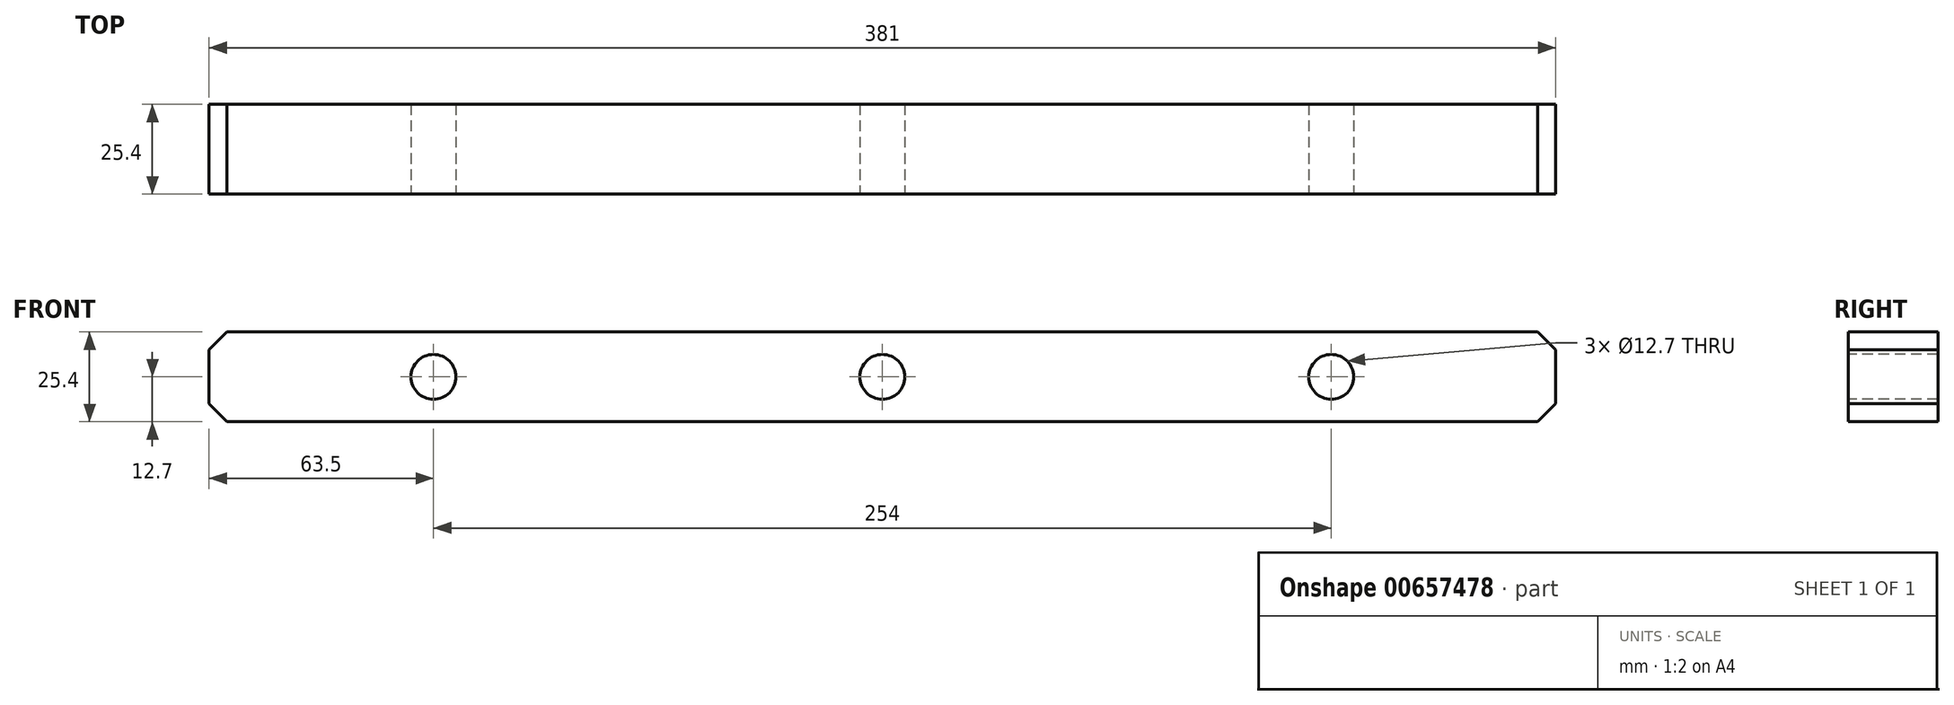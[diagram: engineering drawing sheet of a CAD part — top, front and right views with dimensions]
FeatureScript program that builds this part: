
annotation { "Feature Type Name" : "Feature", "Feature Type Description" : "" }
export const myFeature = defineFeature(function(context is Context, id is Id, definition is map)
    precondition{}
    {
        {
            var Q0;
            Q0=qCreatedBy(makeId("Front.planeOp"),FACE);
            var sketch = newSketch(context, id + "F0", { "sketchPlane" : qUnion([Q0])});
            skLineSegment(sketch, "E0", {"start": v(0, 0) * mm, "end": v(190.5, 0) * mm});
            skLineSegment(sketch, "E1", {"start": v(0, 0) * mm, "end": v(-190.5, 0) * mm});
            skLineSegment(sketch, "E2", {"start": v(-190.5, 0) * mm, "end": v(-190.5, 25.4) * mm});
            skLineSegment(sketch, "E3", {"start": v(190.5, 0) * mm, "end": v(190.5, 25.4) * mm});
            skLineSegment(sketch, "E4", {"start": v(190.5, 25.4) * mm, "end": v(-190.5, 25.4) * mm});
            skSolve(sketch);
        }
        {
            var Q0;
            Q0=makeQuery(id+"F0.imprint","IMPRINT",FACE,{"disambiguationData":[TD([[makeQuery(id+"F0.imprint","IMPRINT",EDGE,{"derivedFrom":sQuery(id+"F0.wireOp",EDGE,"E0")}),1.0]])]});
            extrude(context, id + "F1", {"entities" : qUnion([Q0]), "depth" : 25.4 * mm, "offsetDistance" : 25.4 * mm});
        }
        {
            var Q0;
            Q0=makeQuery(id+"F1.opExtrude","CAP_FACE",FACE,{"disambiguationData":[OSD([sQuery(id+"F0.wireOp",EDGE,"E0"),sQuery(id+"F0.wireOp",EDGE,"E1"),sQuery(id+"F0.wireOp",EDGE,"E2"),sQuery(id+"F0.wireOp",EDGE,"E3"),sQuery(id+"F0.wireOp",EDGE,"E4")])],"isStart":false});
            var sketch = newSketch(context, id + "F2", { "sketchPlane" : qUnion([Q0])});
            skCircle(sketch, "E5", {"center": v(-127, 12.7) * mm, "radius": 6.35 * mm});
            skCircle(sketch, "E6", {"center": v(0, 12.7) * mm, "radius": 6.35 * mm});
            skCircle(sketch, "E7", {"center": v(127, 12.7) * mm, "radius": 6.35 * mm});
            skSolve(sketch);
        }
        {
            var Q0;
            Q0=makeQuery(id+"F2.imprint","IMPRINT",FACE,{"disambiguationData":[TD([[makeQuery(id+"F2.imprint","IMPRINT",EDGE,{"derivedFrom":sQuery(id+"F2.wireOp",EDGE,"E5")}),1.0]])]});
            var Q1;
            Q1=makeQuery(id+"F2.imprint","IMPRINT",FACE,{"disambiguationData":[TD([[makeQuery(id+"F2.imprint","IMPRINT",EDGE,{"derivedFrom":sQuery(id+"F2.wireOp",EDGE,"E6")}),1.0]])]});
            var Q2;
            Q2=makeQuery(id+"F2.imprint","IMPRINT",FACE,{"disambiguationData":[TD([[makeQuery(id+"F2.imprint","IMPRINT",EDGE,{"derivedFrom":sQuery(id+"F2.wireOp",EDGE,"E7")}),1.0]])]});
            var Q3;
            Q3=sQuery(id+"F2.wireOp",EDGE,"E5");
            var Q4;
            Q4=sQuery(id+"F2.wireOp",EDGE,"E6");
            var Q5;
            Q5=sQuery(id+"F2.wireOp",EDGE,"E7");
            extrude(context, id + "F3", {"entities" : qUnion([Q0, Q1, Q2]), "operationType" : NewBodyOperationType.REMOVE, "surfaceEntities" : qUnion([Q3, Q4, Q5]), "oppositeDirection" : true, "depth" : 50.8 * mm, "offsetDistance" : 25.4 * mm});
        }
        {
            var Q0;
            Q0=makeQuery(id+"F1.opExtrude","SWEPT_EDGE",EDGE,{"disambiguationData":[OSD([sQuery(id+"F0.wireOp",EDGE,"E2"),sQuery(id+"F0.wireOp",EDGE,"E4")])]});
            chamfer(context, id + "F4", {"entities" : qUnion([Q0]), "width" : 5.08 * mm, "tangentPropagation" : true});
        }
        {
            var Q0;
            Q0=makeQuery(id+"F1.opExtrude","SWEPT_EDGE",EDGE,{"disambiguationData":[OSD([sQuery(id+"F0.wireOp",EDGE,"E1"),sQuery(id+"F0.wireOp",EDGE,"E2")])]});
            var Q1;
            Q1=makeQuery(id+"F1.opExtrude","SWEPT_EDGE",EDGE,{"disambiguationData":[OSD([sQuery(id+"F0.wireOp",EDGE,"E3"),sQuery(id+"F0.wireOp",EDGE,"E4")])]});
            var Q2;
            Q2=makeQuery(id+"F1.opExtrude","SWEPT_EDGE",EDGE,{"disambiguationData":[OSD([sQuery(id+"F0.wireOp",EDGE,"E0"),sQuery(id+"F0.wireOp",EDGE,"E3")])]});
            chamfer(context, id + "F5", {"entities" : qUnion([Q0, Q1, Q2]), "width" : 5.08 * mm, "tangentPropagation" : true});
        }
    });
